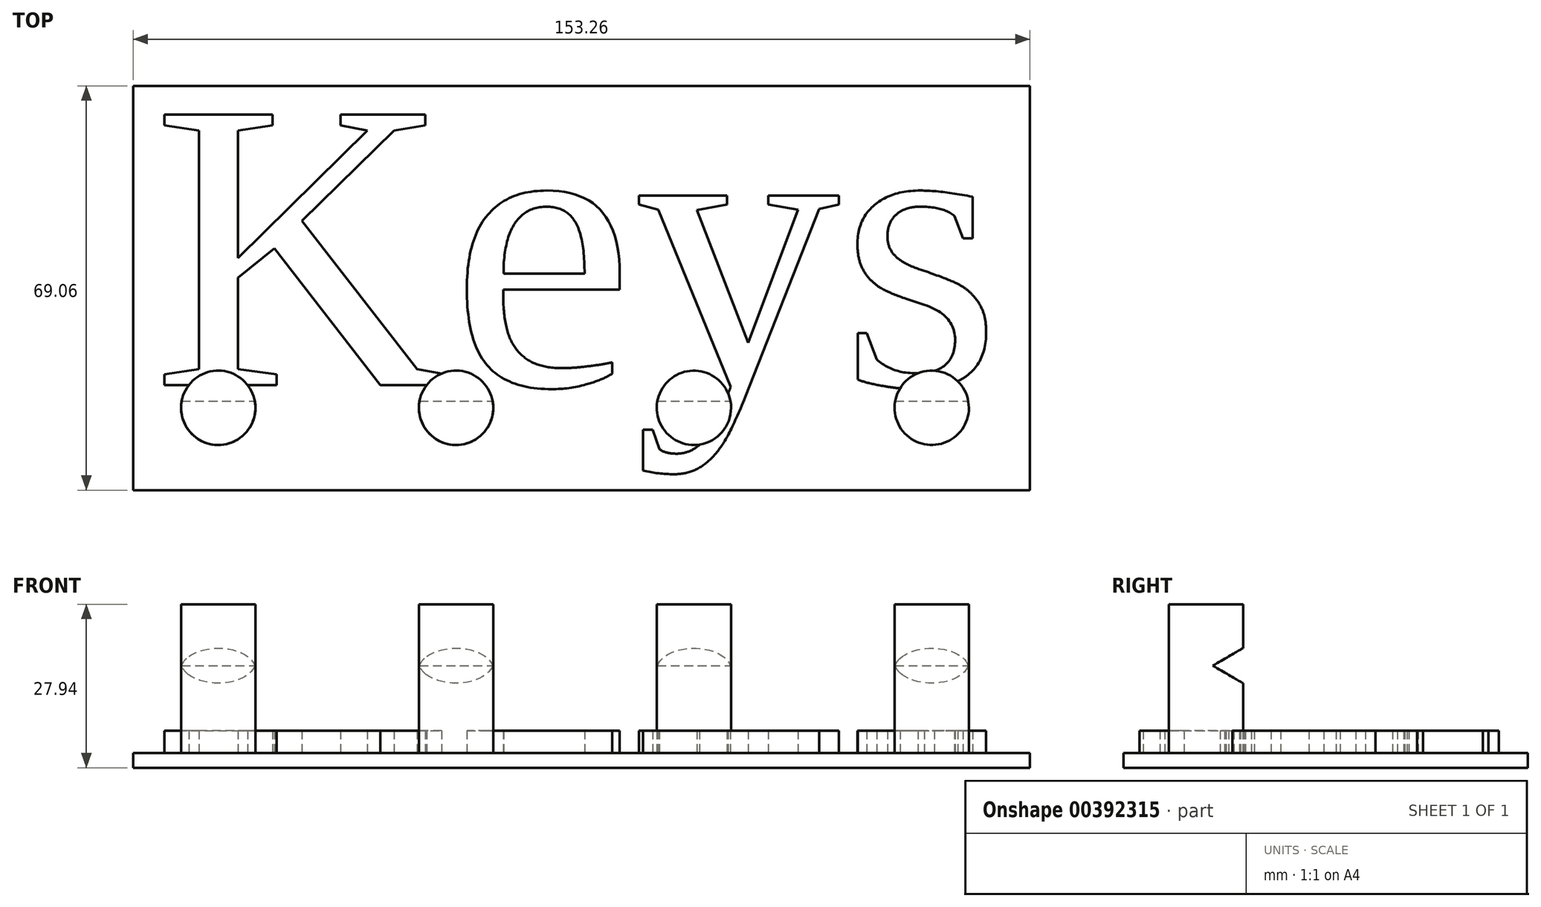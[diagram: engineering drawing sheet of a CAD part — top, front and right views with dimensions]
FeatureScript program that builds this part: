
annotation { "Feature Type Name" : "Feature", "Feature Type Description" : "" }
export const myFeature = defineFeature(function(context is Context, id is Id, definition is map)
    precondition{}
    {
        {
            var Q0;
            Q0=qCreatedBy(makeId("Top.planeOp"),FACE);
            var sketch = newSketch(context, id + "F0", { "sketchPlane" : qUnion([Q0])});
            skText(sketch, "E0", { "text": "Keys", "fontName": "Tinos-Regular.ttf"});
            const initialGuessF0  = {"E0": [-0.07343, 0, 1, 0, 0.0508]};
            skSetInitialGuess(sketch, initialGuessF0);
            skSolve(sketch);
        }
        {
            var Q0;
            Q0=qCreatedBy(makeId("Top.planeOp"),FACE);
            var sketch = newSketch(context, id + "F1", { "sketchPlane" : qUnion([Q0])});
            skCircle(sketch, "E1", {"center": v(-62.2, -3.88) * mm, "radius": 6.35 * mm});
            skCircle(sketch, "E2.1.0.0", {"center": v(-21.56, -3.88) * mm, "radius": 6.35 * mm});
            skCircle(sketch, "E2.2.0.0", {"center": v(19.08, -3.88) * mm, "radius": 6.35 * mm});
            skCircle(sketch, "E2.3.0.0", {"center": v(59.72, -3.88) * mm, "radius": 6.35 * mm});
            skLineSegment(sketch, "E2.direction1", {"start": v(-62.2, -3.88) * mm, "end": v(-21.56, -3.88) * mm, "construction": true});
            skSolve(sketch);
        }
        {
            var Q0;
            Q0=qCreatedBy(makeId("Top.planeOp"),FACE);
            var sketch = newSketch(context, id + "F2", { "sketchPlane" : qUnion([Q0])});
            skLineSegment(sketch, "E3.bottom", {"start": v(-76.75, 51.12) * mm, "end": v(76.51, 51.12) * mm});
            skLineSegment(sketch, "E3.top", {"start": v(-76.75, -17.94) * mm, "end": v(76.51, -17.94) * mm});
            skLineSegment(sketch, "E3.left", {"start": v(-76.75, 51.12) * mm, "end": v(-76.75, -17.94) * mm});
            skLineSegment(sketch, "E3.right", {"start": v(76.51, 51.12) * mm, "end": v(76.51, -17.94) * mm});
            skSolve(sketch);
        }
        {
            var Q0;
            Q0=makeQuery(id+"F2.imprint","IMPRINT",FACE,{"disambiguationData":[TD([[makeQuery(id+"F2.imprint","IMPRINT",EDGE,{"derivedFrom":sQuery(id+"F2.wireOp",EDGE,"E3.bottom")}),-1.0]])]});
            extrude(context, id + "F3", {"entities" : qUnion([Q0]), "oppositeDirection" : true, "depth" : 2.54 * mm});
        }
        {
            var Q0;
            Q0 = qSketchRegion(id + "F0", true);
            extrude(context, id + "F4", {"entities" : qUnion([Q0]), "operationType" : NewBodyOperationType.ADD, "depth" : 3.8 * mm});
        }
        {
            var Q0;
            Q0=makeQuery(id+"F1.imprint","IMPRINT",FACE,{"disambiguationData":[TD([[makeQuery(id+"F1.imprint","IMPRINT",EDGE,{"derivedFrom":sQuery(id+"F1.wireOp",EDGE,"E2.3.0.0")}),1.0]])]});
            var Q1;
            Q1=makeQuery(id+"F1.imprint","IMPRINT",FACE,{"disambiguationData":[TD([[makeQuery(id+"F1.imprint","IMPRINT",EDGE,{"derivedFrom":sQuery(id+"F1.wireOp",EDGE,"E2.1.0.0")}),1.0]])]});
            var Q2;
            Q2=makeQuery(id+"F1.imprint","IMPRINT",FACE,{"disambiguationData":[TD([[makeQuery(id+"F1.imprint","IMPRINT",EDGE,{"derivedFrom":sQuery(id+"F1.wireOp",EDGE,"E2.2.0.0")}),1.0]])]});
            var Q3;
            Q3=makeQuery(id+"F1.imprint","IMPRINT",FACE,{"disambiguationData":[TD([[makeQuery(id+"F1.imprint","IMPRINT",EDGE,{"derivedFrom":sQuery(id+"F1.wireOp",EDGE,"E1")}),1.0]])]});
            extrude(context, id + "F5", {"entities" : qUnion([Q0, Q1, Q2, Q3]), "operationType" : NewBodyOperationType.ADD, "depth" : 25.4 * mm});
        }
        {
            var Q0;
            Q0=qCreatedBy(makeId("Right.planeOp"),FACE);
            var sketch = newSketch(context, id + "F6", { "sketchPlane" : qUnion([Q0])});
            skLineSegment(sketch, "E4", {"start": v(-2.72, 14.9) * mm, "end": v(5.03, 19.38) * mm});
            skLineSegment(sketch, "E5", {"start": v(5.03, 19.38) * mm, "end": v(5.03, 10.42) * mm});
            skLineSegment(sketch, "E6", {"start": v(5.03, 10.42) * mm, "end": v(-2.72, 14.9) * mm});
            skSolve(sketch);
        }
        {
            var Q0;
            Q0=makeQuery(id+"F6.imprint","IMPRINT",FACE,{"disambiguationData":[TD([[makeQuery(id+"F6.imprint","IMPRINT",EDGE,{"derivedFrom":sQuery(id+"F6.wireOp",EDGE,"E4")}),-1.0]])]});
            extrude(context, id + "F7", {"entities" : qUnion([Q0]), "operationType" : NewBodyOperationType.REMOVE, "endBound" : BoundingType.THROUGH_ALL, "oppositeDirection" : true, "depth" : 25.4 * mm, "hasSecondDirection" : true, "secondDirectionBound" : SecondDirectionBoundingType.THROUGH_ALL, "secondDirectionOppositeDirection" : false, "secondDirectionDepth" : 25.4 * mm});
        }
    });
